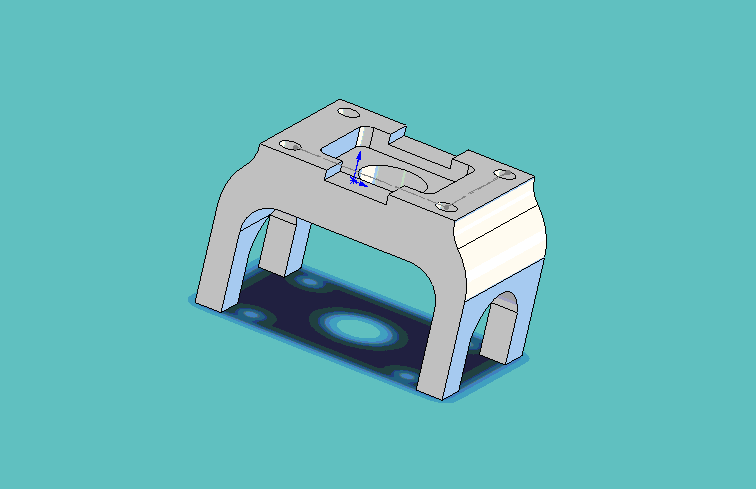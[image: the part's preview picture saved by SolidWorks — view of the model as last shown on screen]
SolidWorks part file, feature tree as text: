
SOLIDWORKS PART (.sldprt)
format: sldprt  version: not decoded by parser v0  size: 411,136 bytes
history: native  units: mm
features: sketch x6, cut_extrude x4, plane x3, fillet x2, material x1, extrude x1, pattern_linear x1 (+10 scaffold rows collapsed)
feature tree (28):
  scaffold x10  (default folders/planes/origin — collapsed)
  material  "Material <not specified>"
  plane  "Frontal"
  plane  "Horizontal"
  plane  "Profile"
  sketch  "Sketch1"  dims[c1.D5=~6.092013mm c1.D1=12.7mm c1.D2=25.4mm c2.D5=12.7mm c2.D9=12.7mm c2.D1=26.035mm c2.D2=3.81mm c2.D3=24.13mm c3.D1=26.035mm c3.D4=26.035mm c3.D5=20.32mm c3.D6=10.16mm c3.D7=36.83mm c3.D8=30.48mm c3.D9=20.32mm c3.D10=3.81mm c3.D11=12.065mm]
  extrude  "Extrude1"  Depth=60.96mm
  sketch  "Sketch4"  dims[D1=19.05mm D2=19.558mm D3=12.7mm D4=35.56mm]
  cut_extrude  "Cut-Extrude1"  [1 undecoded]
  sketch  "Sketch5"  dims[D1=16.002mm D2=16.002mm D3=12.192mm D4=12.192mm]
  cut_extrude  "Cut-Extrude3"  Depth=3.81mm
  fillet  "Fillet1"  Radius=3.556mm
  fillet  "Fillet2"  Radius=3.556mm
  sketch  "Sketch6"  dims[D1=24.13mm D2=18.288mm D3=38.1mm]
  cut_extrude  "Cut-Extrude4"  [1 undecoded]
  sketch  "Sketch7"  dims[D3=~3.510979mm D1=8.255mm D2=7.62mm]
  cut_extrude  "Cut-Extrude5"  [1 undecoded]
  sketch  "Sketch8"
  pattern_linear  "LPattern1"  Count1=2 Count2=2 Spacing1=60.96mm Spacing2=44.45mm
decode coverage: 10 of 14 modeling features carry decoded parameters
note: ~ marks probable driven/reference dimensions
note: 3 parameter values undecoded
summary: no parameter record found for 3 features
note: suppression state not decoded; provenance and decode notes live in map.json
